# Revit family: FP_Revit_18_HPB3011-4_N_Rangehood_90000966B
name_source: partatom
category: Specialty Equipment
revit_build: Autodesk Revit 2018 (Build: 20170223_1515(x64)
units: mm (PartAtom-declared; Revit-internal decimal feet)

## family parameters
Always vertical = Yes
Cut with Voids When Loaded = Yes
OmniClass Number = 23.40.40.00
OmniClass Title = Food Service Equipment and Furnishings
Part Type = Normal
Room Calculation Point = No
Round Connector Dimension = Use Diameter
Shared = No
Work Plane-Based = No

## types (1)
- FP_Revit_18_HPB3011-4_N_Rangehood_90000966B
    Cavity - Depth = 255 mm  [stored 0.836614 ft]
    Cavity - Height = 390 mm  [stored 1.27953 ft]
    Cavity - Width = 705 mm  [stored 2.31299 ft]
    Chassis - Depth = 252 mm  [stored 0.826772 ft]
    Chassis - Height = 380 mm
    Chassis - Width = 700 mm  [stored 2.29659 ft]
    Connector Description - Electrical = 120 V, 15 A, Fused electrical supply
    Connector Description - Extraction = 210mm (8 1/4") Outside diameter of ducting outlet, 400 CFM
    Description = 30" Integrated Insert Rangehood
    Manufacturer = Fisher & Paykel Appliances
    Material - Body = Fisher & Paykel - Stainless Steel
    Material - Glass = Fisher & Paykel - White Bezel
    Model = HPB3011-4_N
    Product - Depth = 280 mm  [stored 0.918635 ft]
    Product - Height = 412 mm  [stored 1.35171 ft]
    Product - Width = 730 mm  [stored 2.39501 ft]
    URL = www.fisherpaykel.com
    Visibility - Clearance Required = Yes

note: [stored X ft] marks values corroborated as IEEE doubles in the binary element streams (Revit-internal decimal feet)

## geometry (parser evidence)
native form markers: Blend x2, Sweep x6
no freeform markers — native parametric forms only
